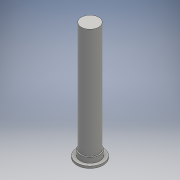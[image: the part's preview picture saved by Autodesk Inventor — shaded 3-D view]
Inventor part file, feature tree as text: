
AUTODESK INVENTOR PART (.ipt)
format: ipt  version: 2016 (Build 200138000, 138)  size: 105,472 bytes
history: native  units: mm
features: extrude x3, sketch x3
ambient origin geometry x8: Origin, YZ Plane, XZ Plane, XY Plane, X Axis, Y Axis, Z Axis, Center Point
bodies: Solid1 (feature_tree)
feature tree (6):
  extrude  "Extrusion1"  Depth=5.08mm TaperAngle=0.0deg
  extrude  "Extrusion2"  Depth=12.7mm TaperAngle=0.0deg
  extrude  "Extrusion3"  Depth=266.7mm TaperAngle=0.0deg
  sketch  "Sketch1"  dims[d0=63.246mm d1=5.08mm d2=0.0mm]
  sketch  "Sketch2"  dims[d3=47.0mm d4=12.7mm d5=0.0mm]
  sketch  "Sketch3"  dims[d6=42.0mm d7=266.7mm d8=0.0mm]
